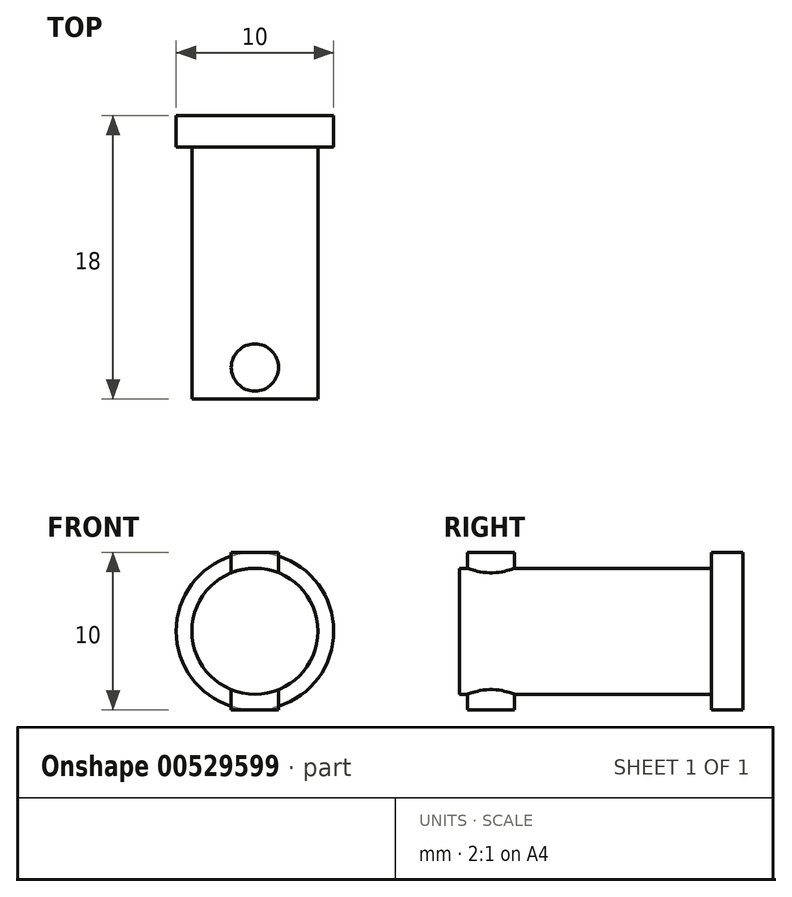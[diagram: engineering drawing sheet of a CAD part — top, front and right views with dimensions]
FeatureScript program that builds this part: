
annotation { "Feature Type Name" : "Feature", "Feature Type Description" : "" }
export const myFeature = defineFeature(function(context is Context, id is Id, definition is map)
    precondition{}
    {
        {
            var Q0;
            Q0=qCreatedBy(makeId("Front.planeOp"),FACE);
            var sketch = newSketch(context, id + "F0", { "sketchPlane" : qUnion([Q0])});
            skCircle(sketch, "E0", {"center": v(0, 0) * mm, "radius": 5 * mm});
            skSolve(sketch);
        }
        {
            var Q0;
            Q0 = qSketchRegion(id + "F0", true);
            extrude(context, id + "F1", {"entities" : qUnion([Q0]), "endBound" : BoundingType.SYMMETRIC, "depth" : 2 * mm, "offsetDistance" : 25 * mm});
        }
        {
            var Q0;
            Q0=makeQuery(id+"F1.opExtrude","CAP_FACE",FACE,{"disambiguationData":[OSD([sQuery(id+"F0.wireOp",EDGE,"E0")])],"isStart":false});
            var sketch = newSketch(context, id + "F2", { "sketchPlane" : qUnion([Q0])});
            skCircle(sketch, "E1", {"center": v(0, 0) * mm, "radius": 4 * mm});
            skSolve(sketch);
        }
        {
            var Q0;
            Q0 = qSketchRegion(id + "F2", true);
            extrude(context, id + "F3", {"entities" : qUnion([Q0]), "operationType" : NewBodyOperationType.ADD, "depth" : 16 * mm, "offsetDistance" : 25 * mm});
        }
        {
            var Q0;
            Q0=qCreatedBy(makeId("Top.planeOp"),FACE);
            var sketch = newSketch(context, id + "F4", { "sketchPlane" : qUnion([Q0])});
            skCircle(sketch, "E2", {"center": v(0, -15) * mm, "radius": 1.5 * mm});
            skSolve(sketch);
        }
        {
            var Q0;
            Q0 = qSketchRegion(id + "F4", true);
            extrude(context, id + "F5", {"entities" : qUnion([Q0]), "operationType" : NewBodyOperationType.ADD, "endBound" : BoundingType.SYMMETRIC, "depth" : 10 * mm, "offsetDistance" : 25 * mm});
        }
    });
